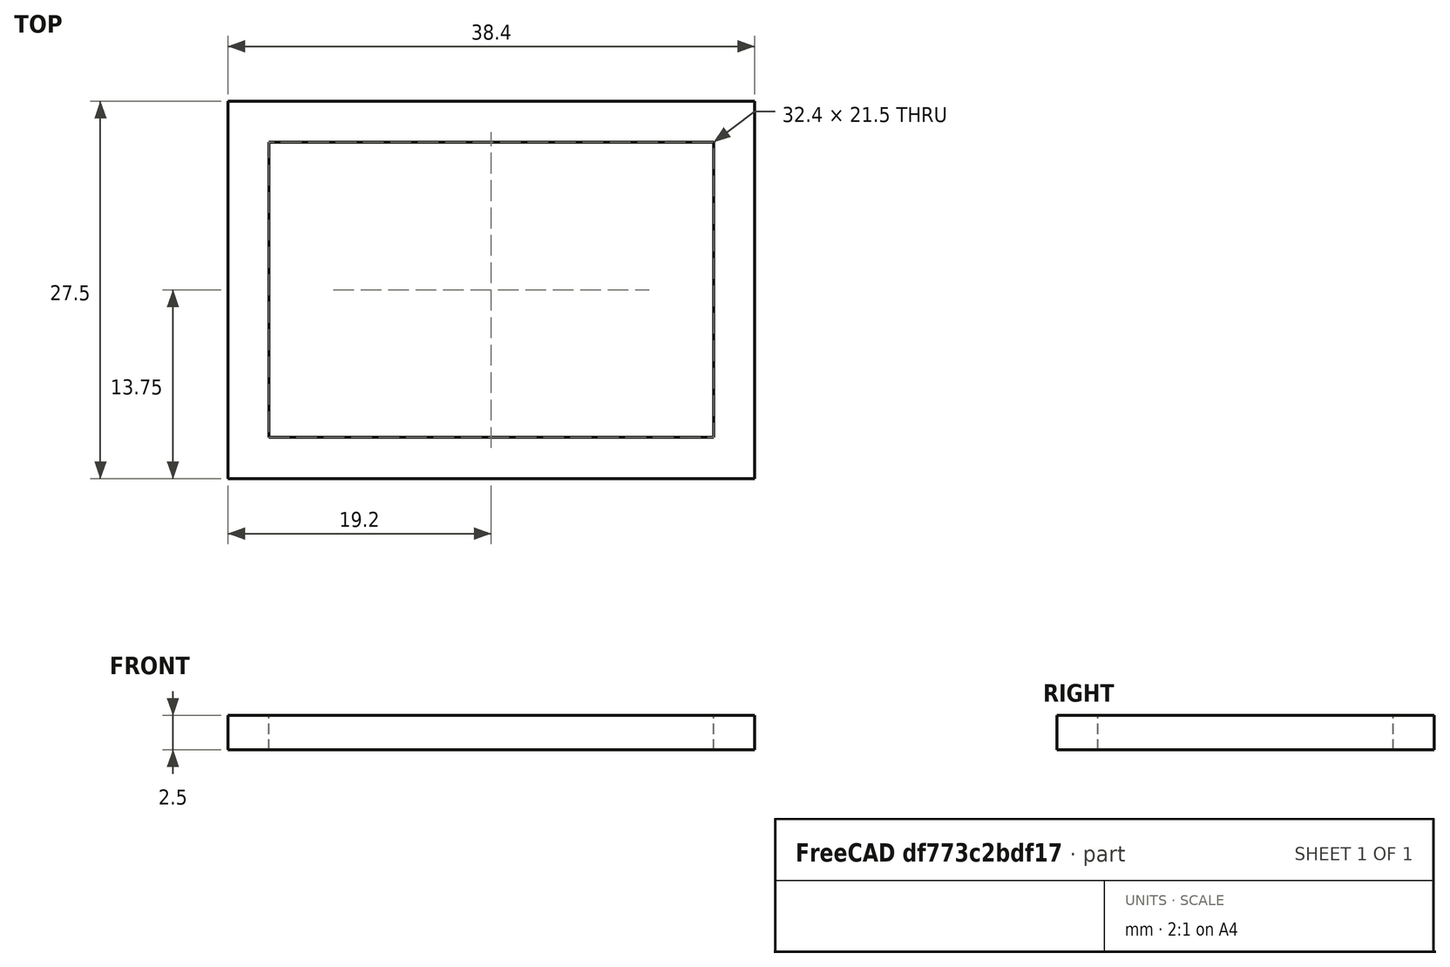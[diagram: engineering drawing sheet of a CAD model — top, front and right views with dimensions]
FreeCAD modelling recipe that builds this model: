
FCSTD DOCUMENT  (FreeCAD 0.15R4671 (Git))
Label: Rubiks Frame Side Motor Shim
License: All rights reserved
LicenseURL: http://en.wikipedia.org/wiki/All_rights_reserved
objects: Sketcher::SketchObject×1, PartDesign::Pad×1
note: 3 computed .brp shape members not serialized (recipe doc carries the construction recipe); baked Part::Feature solids carry a one-line shape summary decoded from their .brp

FEATURE [Sketcher::SketchObject] Sketch
  sketch-geometry (8):
    g0: LineSegment StartX=-19.2 StartY=13.75 StartZ=0 EndX=19.2 EndY=13.75 EndZ=0
    g1: LineSegment StartX=19.2 StartY=13.75 StartZ=0 EndX=19.2 EndY=-13.75 EndZ=0
    g2: LineSegment StartX=19.2 StartY=-13.75 StartZ=0 EndX=-19.2 EndY=-13.75 EndZ=0
    g3: LineSegment StartX=-19.2 StartY=-13.75 StartZ=0 EndX=-19.2 EndY=13.75 EndZ=0
    g4: LineSegment StartX=-16.2 StartY=10.75 StartZ=0 EndX=16.2 EndY=10.75 EndZ=0
    g5: LineSegment StartX=16.2 StartY=10.75 StartZ=0 EndX=16.2 EndY=-10.75 EndZ=0
    g6: LineSegment StartX=16.2 StartY=-10.75 StartZ=0 EndX=-16.2 EndY=-10.75 EndZ=0
    g7: LineSegment StartX=-16.2 StartY=-10.75 StartZ=0 EndX=-16.2 EndY=10.75 EndZ=0
  constraints (24):
    c: Coincident(g0,g1)
    c: Coincident(g1,g2)
    c: Coincident(g2,g3)
    c: Coincident(g3,g0)
    c: Horizontal(g0)
    c: Horizontal(g2)
    c: Vertical(g1)
    c: Vertical(g3)
    c: Distance(g3) = 27.5
    c: Distance(g0) = 38.4
    c: Symmetric(g0,g0,g-2)
    c: Symmetric(g0,g2,g-1)
    c: Coincident(g4,g5)
    c: Coincident(g5,g6)
    c: Coincident(g6,g7)
    c: Coincident(g7,g4)
    c: Horizontal(g4)
    c: Horizontal(g6)
    c: Vertical(g5)
    c: Vertical(g7)
    c: DistanceX(g4,g0) = -3
    c: DistanceY(g4,g0) = 3
    c: DistanceX(g5,g1) = 3
    c: DistanceY(g5,g1) = -3
FEATURE [PartDesign::Pad] Pad
  Length = 2.5
  Length2 = 100
  Sketch = -> Sketch
  Type = 0
